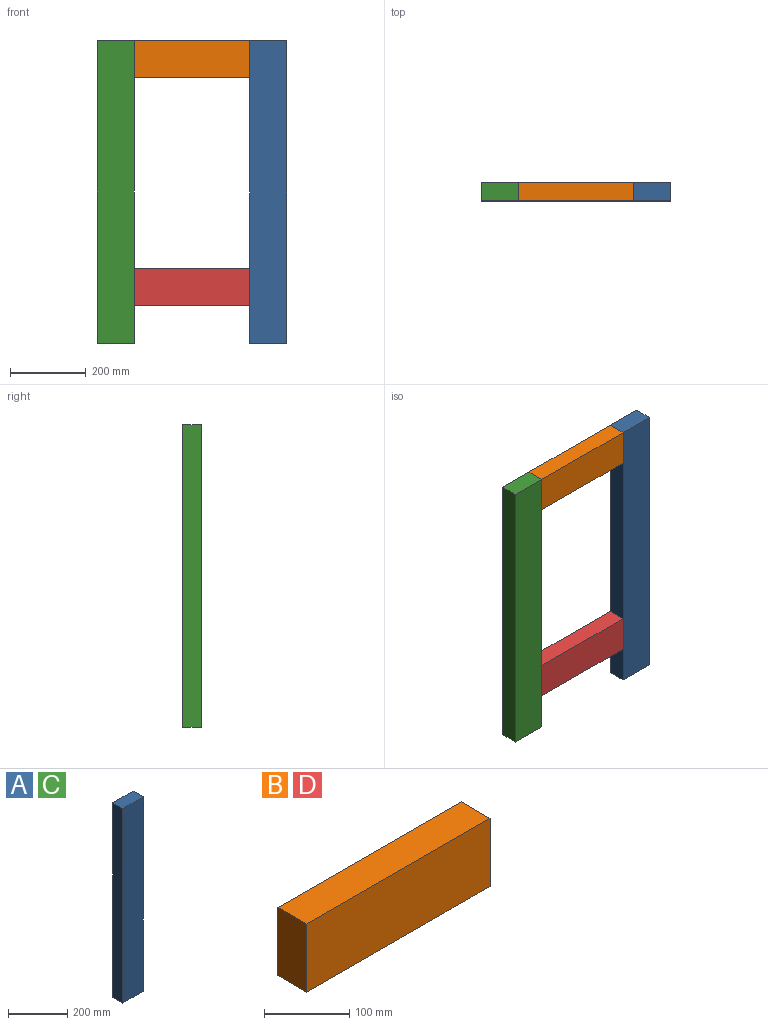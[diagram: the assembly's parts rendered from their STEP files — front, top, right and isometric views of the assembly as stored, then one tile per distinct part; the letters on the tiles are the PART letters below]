
ASSEMBLY  parts=4 mates=3
PART A: 6 faces, bbox 98x48x800 mm
  f0: plane 800x48mm, normal (-1,0,0), area 38400mm2, adj f1,f3,f4,f5
  f1: plane 98x48mm, normal (0,0,-1), area 4704mm2, adj f0,f2,f4,f5
  f2: plane 800x48mm, normal (1,0,0), area 38400mm2, adj f1,f3,f4,f5
  f3: plane 98x48mm, normal (0,0,1), area 4704mm2, adj f0,f2,f4,f5
  f4: plane 800x98mm, normal (0,-1,0), area 78400mm2, adj f0,f1,f2,f3
  f5: plane 800x98mm, normal (0,1,0), area 78400mm2, adj f0,f1,f2,f3
PART B: 6 faces, bbox 304x48x98 mm
  f0: plane 304x48mm, normal (0,0,1), area 14592mm2, adj f1,f3,f4,f5
  f1: plane 98x48mm, normal (-1,0,0), area 4704mm2, adj f0,f2,f4,f5
  f2: plane 304x48mm, normal (0,0,-1), area 14592mm2, adj f1,f3,f4,f5
  f3: plane 98x48mm, normal (1,0,0), area 4704mm2, adj f0,f2,f4,f5
  f4: plane 304x98mm, normal (0,-1,0), area 29792mm2, adj f0,f1,f2,f3
  f5: plane 304x98mm, normal (0,1,0), area 29792mm2, adj f0,f1,f2,f3
PART C: same geometry as A
PART D: same geometry as B
PLACE A t=(-301.21,23.82,-181.85)mm
PLACE B t=(-453.21,23.82,520.15)mm
PLACE C t=(-703.21,23.82,-181.85)mm
PLACE D t=(-453.21,23.82,-81.85)mm
MATE fastened C.f3 <-> B.f0  axis (0,0,1) through (-605.21,23.82,618.15)mm
MATE fastened B.f0 <-> A.f3  axis (0,0,1) through (-301.21,23.82,618.15)mm
MATE fastened D.f3 <-> A.f0  axis (1,0,0) through (-301.21,-24.18,-81.85)mm
